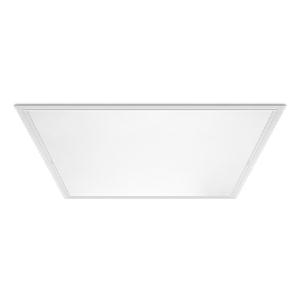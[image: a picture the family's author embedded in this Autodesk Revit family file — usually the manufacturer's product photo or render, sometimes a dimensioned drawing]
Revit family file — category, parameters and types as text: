
# Revit family: 3f_filippi_-_l_600_luce_diffusa_vs_3f_filippi_-_22858_-_l_600_42w-840_dali_vs_596x596
name_source: partatom
category: Lighting Fixtures
units: mm (PartAtom-declared; Revit-internal decimal feet)

## family parameters
Cut with Voids When Loaded = No
Host = Face
Light Source = No
Part Type = Normal
Room Calculation Point = No
Round Connector Dimension = Use Diameter
Shared = No

## types (1)
- 3F Filippi - L 600 Luce Diffusa VS (1 x LED, 5612 lm, 45 W, 4000 K)
    Apparent Load = 45 VA
    Approval mark = ENEC
    CIE Flux Codes = 63 92 98 100 100
    Color Rendering = 80
    Color Temperature = 4000 K
    Control Gear = Electronic transformer
    Default Elevation = 1800 mm
    Description = ILLUMINOTECHNICAL
Luminous efficiency 100% (DLOR 100%, ULOR 0%).
Initial luminous flux of the luminaire 5612 lm.
Direct symmetric distribution.
Installation Interdistance Transv.D = 1.17 x hu - Long.D = 1.16 x hu.
Average luminance <3000 cd/m² for radial angles >65°.
Tabular UGR (CIE 117 - 4H-8H; S=0.25H; 70/50/20): RUG 18.2 - 18.
Beam angle: 90° - 88°.
Luminous efficacy 125 lm/W.
Lifetime (L93/B10): 30000 h. (tq+25°C)
Lifetime (L90/B10): 50000 h. (tq+25°C)
Lifetime (L85/B10): 80000 h. (tq+25°C)
Lifetime (L80/B10): 100000 h. (tq+25°C)
Sudden decreased luminous flux after 50000 hours: 0% (C0).
Photobiological safety in compliance with IEC/TR 62778: RG0 risk exempt, (IEC 62471).
In compliance with IEC/EN 62722-2-1 - IEC/EN 62717 standards.

SOURCE
Squared LED module 42W/840.
Source with special protection against aggressive chemically-volatile substances for standard LED technology.
Energy efficiency class (UE 2019/2020 - UE 2019/2015): D.
CIE 13.3 Colour rendering index: CRI >80 (R9 <50%).
IES TM-30 Fidelity Index: Rf = 84 Rg = 95.
CCT nominal colour temperature 4000 K.
Colour initial tolerance (MacAdam): SDCM 3.

MECHANICAL
Housing in galvannealed steel, painted in white epoxy-polyester.
Perimetral frame in white polycarbonate.
VS moulded glass, anti-glare, tempered, non-combustible, thickness 4 mm.
Anti-glare opal polycarbonate filter for brightness uniformity.
Luminaire with limited surface temperature. - D - (EN 60598-2-24)
Dimensions: 596x596 mm, height 95 mm. Weight 7.1 kg.
IP65 protection degree for exposed part, IP64 for recessed part.
Mechanical strength to impacts IK08 (5 joule).
Glow-wire test resistance 960°C.

ELECTRICAL
Halogen Free DALI-2, PUSH-DIM, electronic wiring 230V-50/60Hz, power factor 0.95 at full load, THD <25%, constant output current, class I, 1 driver, 1 DALI addresse.
Power of the luminaire 45 W.
CE - IEC 60598-1 - EN 60598-1.
SAFE FLICKER: PstLM=<1 and SVM=<0.4 (IEC TR 61547-1 and IEC TR 63158), to ensure a more comfortable and safe light.
Luminaire compliant with EN 60598-2-22 for power supply from a centralised emergency system CPSS (Central Power Supply System), not incorporated in the luminaire - high risk areas excluded. The default power and flux are 100% in AC and 15% in DC.
Ambient temperature from 0°C to +40°C.
Temperature class T6 max 85°C.
5-pole terminal block (L-N-PE-DA/DA) quick connection for line connection with connection capacity 2x2.5 mm² per poles.
Relative humidity UR: <85%.

INSTALLATION
Lay-on or pull-up recessed fitting using frame and anti-fall safety cable accessories.
All accessories dedicated to this product are available on the Catalog and on our website www.3F-Filippi.com.

APPLICATIONS
In environments requiring protection and simplified cleaning.
Hospitals, pharmaceutical, chemical, aseptic laboratories, sterilised rooms.
Environments with VDTs.
Environments where demanding visual tasks are performed and soft diffuse light is required for optimal visual comfort and total shielding of the light source.

LIGHT MANAGEMENT
Recommended minimum setting: 10%.
The device, equipped with DALI-2 driver, can be controlled manually with 3F Easy Dim technology or automatically/manually with 3F Smart Dimming technology and/or centralised DALI systems.
DALI-2 certification guarantees interoperability with other devices with the same certification.
In electrical systems without a regulation system (manual or automatic) and DALI bus, a suitable jumper must be made on the DA-DA terminals of the appliance.

WARNING
Luminaire designed for disposal/recycling at end-of-life.
Replaceable (LED only) light source by a professional. Replaceable control gear by a professional.
    Height = 0 mm  [stored 0 ft]
    Lamp = 1 x LED
    Lamp Light Flux = 5612 lm
    Lamp Power = 45 W
    Lamp count = 1
    Length = 596 mm
    Lifetime = 50000 h
    Luminous efficacy = 125 lm/W
    Manufacturer = 3F Filippi
    ModVariant = No
    Model = 3F Filippi - 22858 - L 600 42W-840 DALI VS 596x596
    Mounting Place = Ceiling
    Mounting Type = Recessed
    Number of Poles = 1
    OnlyDefault = Yes
    Power Factor = 1
    Product Name = 3F Filippi - L 600 Luce Diffusa VS
    Product group = recessed luminaire
    ProductGroupID = 4
    Protection Class = Protection class I
    Protection Degree = IP 64
    RLX_Detail_Level = 1
    RLX_Emergency_Light_Flux = 0 lm
    RLX_Emergency_Type = 0
    RLX_Emergency_Type_DB = No
    RlxData = <blob elided: 128205 chars, md5=302bbec3>
    Socket = socket
    Standby Power = 0 W
    System Light Flux = 5612 lm
    System Power = 45 W
    Type Comments = Product without accessories
    Type Image = 3ffilippi_l_600_luce_diffusa_vs.jpg
    URL = http://relux.com
    VarID = ---
    Voltage = 0 V
    Weight = 0.00 kg
    Width = 596 mm

note: [stored X ft] marks values corroborated as IEEE doubles in the binary element streams (Revit-internal decimal feet)

## geometry (parser evidence)
native form markers: Blend x4, Sweep x11
no freeform markers — native parametric forms only
